# Revit family: Basin-Wheelchair_Users_Lavatory-American_Standard-914X.XXX_Series
name_source: partatom
category: Plumbing Fixtures
units: mm (PartAtom-declared; Revit-internal decimal feet)

## family parameters
Cut with Voids When Loaded = No
Host = Face
OmniClass Number = 23.45.05.14.14
OmniClass Title = Sinks/Lavatories
Part Type = Normal
Room Calculation Point = No
Round Connector Dimension = Use Radius
Shared = Yes

## types (5) — shared parameters
ADA Compliant = Yes
Assembly Code = D2010310
Basin Shape = Rectangle
CW Connection = Yes
CWFU = 1.5
Centre Hole Extrusion = 6 5/8"
Cold Water Connection Diameter = 3/8"
Cold Water Connection Radius = 3/16"
Default Elevation = 34"
Finish = Vitreous China-American Standard-020-White
HW Connection = Yes
HWFU = 1.5
Height = 6 5/8"
Hot Water Connection Diameter = 3/8"
Hot Water Connection Radius = 3/16"
Installation Type = Wall Mounted
Length = 27"
Manufacturer = American Standard
Masterformat Title = Commercial Lavatories and Sinks
Material = Vitreous China-American Standard-020-White
Price = Prices may vary. Please consult Manufacturer Representative for most up-to-date price list.
Product Documentation Link = https://americanstandard.box.com
Product Page URL = https://www.americanstandard-us.com
Revised Date = 09/15/2021
URL = http://www.americanstandard-us.com
Vent Connection = No
WFU = 2
Waste Connection = Yes
Waste Connection Diameter = 1 1/4"
Waste Connection Radius = 5/8"
Width = 20"

## per-type parameters (varying)
| type | C/H Hole | Connection C/H Distance | Description | Extra Hole | Extra Hole Distance | Extra Hole Void Extrusion | Faucet C/W Distance | Faucet Distance to the Wall | H/C Water Void Extrusion | Less Over Flow | Overflow Hole Extrusion |
| 9141.011 | Yes | 8" | Wheelchair users lavatory. | No | 5" | -3" | 4" | 7 1/8" | 9" | No | 26" |
| 9141.911 | Yes | 8" | Wheelchair users lavatory. Less overflow. | No | 5" | -3" | 4" | 7 1/8" | 9" | Yes | 24" |
| 9140.021 | Yes | 10 1/2" | Wheelchair users lavatory. | Yes | 2 3/4" | 7 3/16" | 10 1/2" | 8 5/8" | 9" | No | 26" |
| 9140.013 | Yes | 10 1/2" | Wheelchair users lavatory | No | 2 3/4" | -3" | 10 1/2" | 8 5/8" | 9" | No | 26" |
| 9140.047 | No | 10 1/2" | Wheelchair users lavatory | No | 5" | -3" | 10" | 8 5/8" | -1" | No | 26" |

note: column(s) folded — value = type name in every type: Model

## geometry (parser evidence)
native form markers: Extrusion x4, Sweep x2
no freeform markers — native parametric forms only
